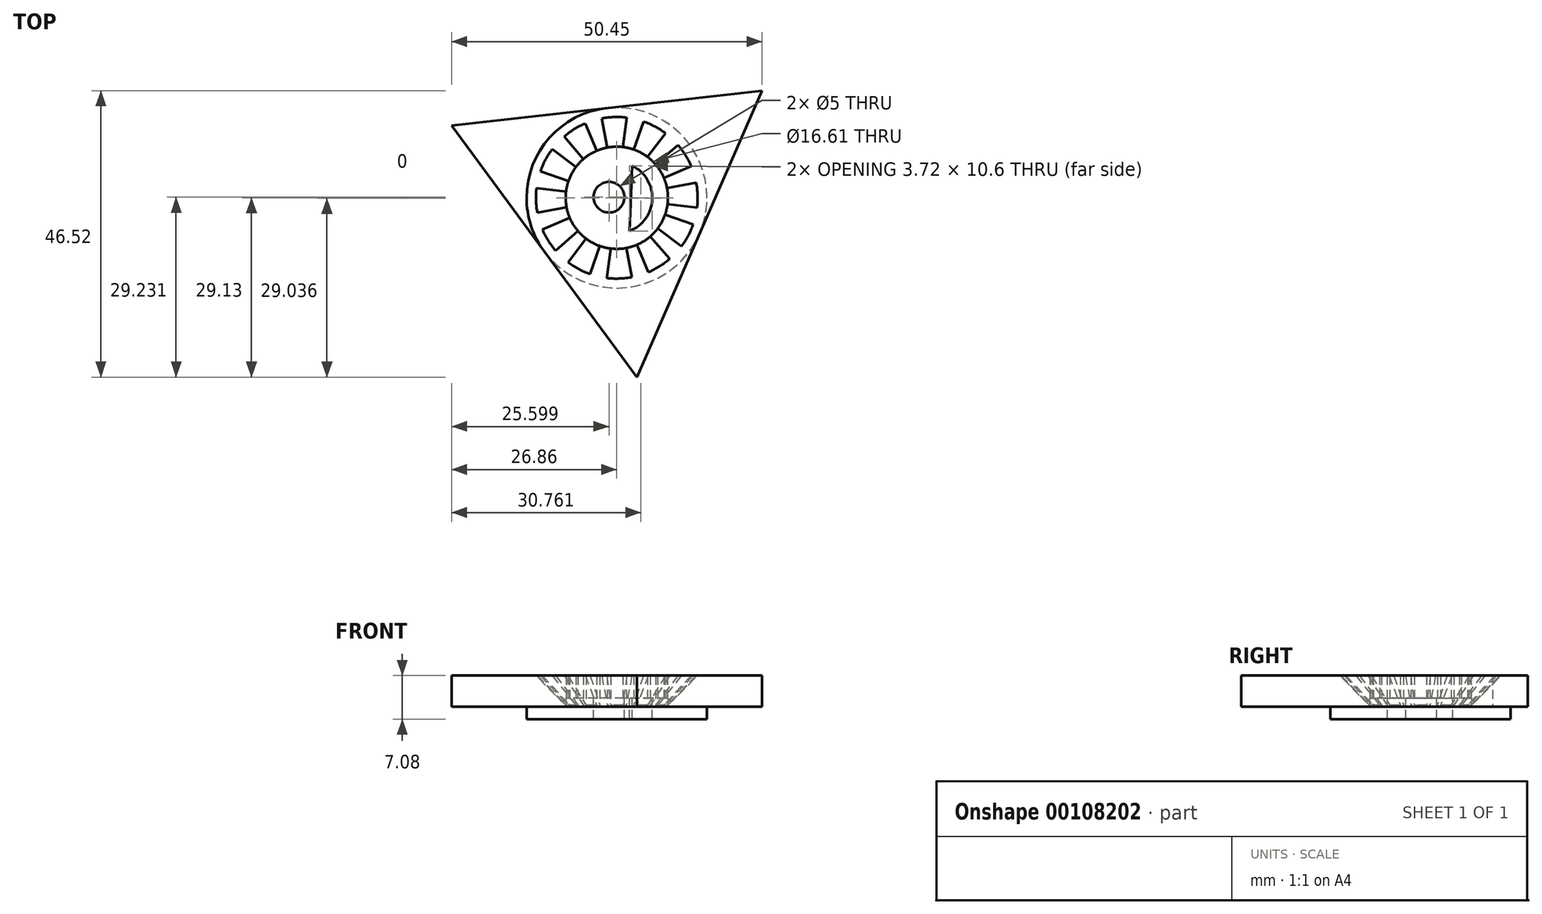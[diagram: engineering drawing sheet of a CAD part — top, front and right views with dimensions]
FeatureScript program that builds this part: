
annotation { "Feature Type Name" : "Feature", "Feature Type Description" : "" }
export const myFeature = defineFeature(function(context is Context, id is Id, definition is map)
    precondition{}
    {
        {
            var Q0;
            Q0=qCreatedBy(makeId("Top.planeOp"),FACE);
            var sketch = newSketch(context, id + "F0", { "sketchPlane" : qUnion([Q0])});
            skCircle(sketch, "E0", {"center": v(0, 0) * mm, "radius": 14.66 * mm});
            skCircle(sketch, "E1.cCircle", {"center": v(0, 0) * mm, "radius": 14.66 * mm, "construction": true});
            skLineSegment(sketch, "E1.0", {"start": v(23.6, 17.4) * mm, "end": v(3.27, -29.13) * mm});
            skLineSegment(sketch, "E1.1", {"start": v(3.27, -29.13) * mm, "end": v(-26.86, 11.73) * mm});
            skLineSegment(sketch, "E1.2", {"start": v(-26.86, 11.73) * mm, "end": v(23.6, 17.4) * mm});
            skPoint(sketch, "E1.0.midPoint", {"position": v(13.43, -5.87) * mm});
            skCircle(sketch, "E2", {"center": v(0, 0) * mm, "radius": 8.3 * mm});
            skSolve(sketch);
        }
        {
            var Q0;
            {var subQ0=sQuery(id+"F0.wireOp",EDGE,"E1.1");var subQ1=sQuery(id+"F0.wireOp",EDGE,"E0");var subQ2=makeQuery(id+"F0.imprint","INTERSECT",VERTEX,{"derivedFrom":[subQ1,subQ0]});Q0=makeQuery(id+"F0.imprint","IMPRINT",FACE,{"disambiguationData":[TD([[makeQuery(id+"F0.imprint","IMPRINT",EDGE,{"disambiguationData":[TD([[subQ2,1.0]])],"derivedFrom":subQ1}),-1.0]])]});}
            var Q1;
            {var subQ0=sQuery(id+"F0.wireOp",EDGE,"7ad4a74b-b42f-41d7-8abd-379b6c7fd1b9.3.0");Q1=makeQuery(id+"F0.imprint","IMPRINT",FACE,{"disambiguationData":[TD([[makeQuery(id+"F0.imprint","IMPRINT",EDGE,{"derivedFrom":subQ0}),-1.0]])]});}
            var Q2;
            {var subQ0=sQuery(id+"F0.wireOp",EDGE,"kC1Kmy56-I1pg-bns6-OiFE-b4c0AROArugu");Q2=makeQuery(id+"F0.imprint","IMPRINT",FACE,{"disambiguationData":[TD([[makeQuery(id+"F0.imprint","IMPRINT",EDGE,{"derivedFrom":subQ0}),-1.0]])]});}
            var Q3;
            {var subQ0=sQuery(id+"F0.wireOp",EDGE,"7ad4a74b-b42f-41d7-8abd-379b6c7fd1b9.7.0");Q3=makeQuery(id+"F0.imprint","IMPRINT",FACE,{"disambiguationData":[TD([[makeQuery(id+"F0.imprint","IMPRINT",EDGE,{"derivedFrom":subQ0}),-1.0]])]});}
            var Q4;
            {var subQ0=sQuery(id+"F0.wireOp",EDGE,"7ad4a74b-b42f-41d7-8abd-379b6c7fd1b9.6.0");Q4=makeQuery(id+"F0.imprint","IMPRINT",FACE,{"disambiguationData":[TD([[makeQuery(id+"F0.imprint","IMPRINT",EDGE,{"derivedFrom":subQ0}),-1.0]])]});}
            var Q5;
            {var subQ0=sQuery(id+"F0.wireOp",EDGE,"E1.1");var subQ1=sQuery(id+"F0.wireOp",EDGE,"E0");var subQ2=makeQuery(id+"F0.imprint","INTERSECT",VERTEX,{"derivedFrom":[subQ1,subQ0]});Q5=makeQuery(id+"F0.imprint","IMPRINT",FACE,{"disambiguationData":[TD([[makeQuery(id+"F0.imprint","IMPRINT",EDGE,{"disambiguationData":[TD([[subQ2,-1.0]])],"derivedFrom":subQ1}),-1.0]])]});}
            var Q6;
            {var subQ15=sQuery(id+"F0.wireOp",EDGE,"E0");var subQ18=makeQuery(id+"F0.imprint","INTERSECT",VERTEX,{"derivedFrom":[subQ15,sQuery(id+"F0.wireOp",EDGE,"E1.1")]});Q6=makeQuery(id+"F0.imprint","IMPRINT",FACE,{"disambiguationData":[TD([[makeQuery(id+"F0.imprint","IMPRINT",EDGE,{"disambiguationData":[TD([[subQ18,1.0]])],"derivedFrom":subQ15}),1.0]])]});}
            var Q7;
            {var subQ0=sQuery(id+"F0.wireOp",EDGE,"7ad4a74b-b42f-41d7-8abd-379b6c7fd1b9.8.0");Q7=makeQuery(id+"F0.imprint","IMPRINT",FACE,{"disambiguationData":[TD([[makeQuery(id+"F0.imprint","IMPRINT",EDGE,{"derivedFrom":subQ0}),-1.0]])]});}
            var Q8;
            {var subQ0=sQuery(id+"F0.wireOp",EDGE,"7ad4a74b-b42f-41d7-8abd-379b6c7fd1b9.1.0");Q8=makeQuery(id+"F0.imprint","IMPRINT",FACE,{"disambiguationData":[TD([[makeQuery(id+"F0.imprint","IMPRINT",EDGE,{"derivedFrom":subQ0}),-1.0]])]});}
            var Q9;
            {var subQ0=sQuery(id+"F0.wireOp",EDGE,"7ad4a74b-b42f-41d7-8abd-379b6c7fd1b9.5.0");Q9=makeQuery(id+"F0.imprint","IMPRINT",FACE,{"disambiguationData":[TD([[makeQuery(id+"F0.imprint","IMPRINT",EDGE,{"derivedFrom":subQ0}),-1.0]])]});}
            var Q10;
            {var subQ0=sQuery(id+"F0.wireOp",EDGE,"7ad4a74b-b42f-41d7-8abd-379b6c7fd1b9.10.0");Q10=makeQuery(id+"F0.imprint","IMPRINT",FACE,{"disambiguationData":[TD([[makeQuery(id+"F0.imprint","IMPRINT",EDGE,{"derivedFrom":subQ0}),-1.0]])]});}
            var Q11;
            {var subQ0=sQuery(id+"F0.wireOp",EDGE,"7ad4a74b-b42f-41d7-8abd-379b6c7fd1b9.11.0");Q11=makeQuery(id+"F0.imprint","IMPRINT",FACE,{"disambiguationData":[TD([[makeQuery(id+"F0.imprint","IMPRINT",EDGE,{"derivedFrom":subQ0}),-1.0]])]});}
            var Q12;
            {var subQ0=sQuery(id+"F0.wireOp",EDGE,"7ad4a74b-b42f-41d7-8abd-379b6c7fd1b9.4.0");Q12=makeQuery(id+"F0.imprint","IMPRINT",FACE,{"disambiguationData":[TD([[makeQuery(id+"F0.imprint","IMPRINT",EDGE,{"derivedFrom":subQ0}),-1.0]])]});}
            var Q13;
            {var subQ0=sQuery(id+"F0.wireOp",EDGE,"7ad4a74b-b42f-41d7-8abd-379b6c7fd1b9.9.0");Q13=makeQuery(id+"F0.imprint","IMPRINT",FACE,{"disambiguationData":[TD([[makeQuery(id+"F0.imprint","IMPRINT",EDGE,{"derivedFrom":subQ0}),-1.0]])]});}
            var Q14;
            {var subQ0=sQuery(id+"F0.wireOp",EDGE,"E1.2");var subQ1=sQuery(id+"F0.wireOp",EDGE,"E0");var subQ2=makeQuery(id+"F0.imprint","INTERSECT",VERTEX,{"derivedFrom":[subQ1,subQ0]});Q14=makeQuery(id+"F0.imprint","IMPRINT",FACE,{"disambiguationData":[TD([[makeQuery(id+"F0.imprint","IMPRINT",EDGE,{"disambiguationData":[TD([[subQ2,1.0]])],"derivedFrom":subQ1}),-1.0]])]});}
            var Q15;
            {var subQ0=sQuery(id+"F0.wireOp",EDGE,"7ad4a74b-b42f-41d7-8abd-379b6c7fd1b9.2.0");Q15=makeQuery(id+"F0.imprint","IMPRINT",FACE,{"disambiguationData":[TD([[makeQuery(id+"F0.imprint","IMPRINT",EDGE,{"derivedFrom":subQ0}),-1.0]])]});}
            extrude(context, id + "F1", {"entities" : qUnion([Q0, Q1, Q2, Q3, Q4, Q5, Q6, Q7, Q8, Q9, Q10, Q11, Q12, Q13, Q14, Q15]), "depth" : 5.08 * mm});
        }
        {
            var Q0;
            Q0=makeQuery(id+"F1.opExtrude","CAP_EDGE",EDGE,{"disambiguationData":[OSD([sQuery(id+"F0.wireOp",EDGE,"E2")])],"isStart":false});
            chamfer(context, id + "F2", {"entities" : qUnion([Q0]), "width" : 4.83 * mm, "tangentPropagation" : true});
        }
        {
            var Q0;
            Q0=makeQuery(id+"F1.opExtrude","CAP_FACE",FACE,{"disambiguationData":[OSD([sQuery(id+"F0.wireOp",EDGE,"E1.0"),sQuery(id+"F0.wireOp",EDGE,"E1.1"),sQuery(id+"F0.wireOp",EDGE,"E1.2"),sQuery(id+"F0.wireOp",EDGE,"E2")])],"isStart":true});
            var sketch = newSketch(context, id + "F3", { "sketchPlane" : qUnion([Q0])});
            skCircle(sketch, "E3.0", {"center": v(0, 0) * mm, "radius": 8.3 * mm});
            skLineSegment(sketch, "E3.1", {"start": v(-26.86, -11.73) * mm, "end": v(23.6, -17.4) * mm});
            skLineSegment(sketch, "E3.2", {"start": v(3.27, 29.13) * mm, "end": v(-26.86, -11.73) * mm});
            skLineSegment(sketch, "E3.3", {"start": v(23.6, -17.4) * mm, "end": v(3.27, 29.13) * mm});
            skCircle(sketch, "E4.0", {"center": v(0, 0) * mm, "radius": 14.66 * mm});
            skLineSegment(sketch, "E5", {"start": v(-5, 6.64) * mm, "end": v(-8.81, 11.71) * mm});
            skLineSegment(sketch, "E6", {"start": v(-6.3, 5.42) * mm, "end": v(-11.1, 9.57) * mm});
            skLineSegment(sketch, "E7.1.0", {"start": v(-8.16, 1.55) * mm, "end": v(-14.4, 2.73) * mm});
            skLineSegment(sketch, "E7.1.1", {"start": v(-7.64, 3.25) * mm, "end": v(-13.49, 5.74) * mm});
            skLineSegment(sketch, "E7.2.0", {"start": v(-7.84, -2.74) * mm, "end": v(-13.84, -4.83) * mm});
            skLineSegment(sketch, "E7.2.1", {"start": v(-8.24, -1) * mm, "end": v(-14.55, -1.78) * mm});
            skLineSegment(sketch, "E7.3.0", {"start": v(-5.42, -6.3) * mm, "end": v(-9.57, -11.1) * mm});
            skLineSegment(sketch, "E7.3.1", {"start": v(-6.64, -5) * mm, "end": v(-11.71, -8.81) * mm});
            skLineSegment(sketch, "E7.4.0", {"start": v(-1.55, -8.16) * mm, "end": v(-2.73, -14.4) * mm});
            skLineSegment(sketch, "E7.4.1", {"start": v(-3.25, -7.64) * mm, "end": v(-5.74, -13.49) * mm});
            skLineSegment(sketch, "E7.5.0", {"start": v(2.74, -7.84) * mm, "end": v(4.83, -13.84) * mm});
            skLineSegment(sketch, "E7.5.1", {"start": v(1, -8.24) * mm, "end": v(1.78, -14.55) * mm});
            skLineSegment(sketch, "E7.6.0", {"start": v(6.3, -5.42) * mm, "end": v(11.1, -9.57) * mm});
            skLineSegment(sketch, "E7.6.1", {"start": v(5, -6.64) * mm, "end": v(8.81, -11.71) * mm});
            skLineSegment(sketch, "E7.7.0", {"start": v(8.16, -1.55) * mm, "end": v(14.4, -2.73) * mm});
            skLineSegment(sketch, "E7.7.1", {"start": v(7.64, -3.25) * mm, "end": v(13.49, -5.74) * mm});
            skLineSegment(sketch, "E7.8.0", {"start": v(7.84, 2.74) * mm, "end": v(13.84, 4.83) * mm});
            skLineSegment(sketch, "E7.8.1", {"start": v(8.24, 1) * mm, "end": v(14.55, 1.78) * mm});
            skLineSegment(sketch, "E7.9.0", {"start": v(5.42, 6.3) * mm, "end": v(9.57, 11.1) * mm});
            skLineSegment(sketch, "E7.9.1", {"start": v(6.64, 5) * mm, "end": v(11.71, 8.81) * mm});
            skLineSegment(sketch, "E7.10.0", {"start": v(1.55, 8.16) * mm, "end": v(2.73, 14.4) * mm});
            skLineSegment(sketch, "E7.10.1", {"start": v(3.25, 7.64) * mm, "end": v(5.74, 13.49) * mm});
            skLineSegment(sketch, "E7.11.0", {"start": v(-2.74, 7.84) * mm, "end": v(-4.83, 13.84) * mm});
            skLineSegment(sketch, "E7.11.1", {"start": v(-1, 8.24) * mm, "end": v(-1.78, 14.55) * mm});
            skLineSegment(sketch, "E8", {"start": v(3.25, 7.64) * mm, "end": v(-3.25, -7.64) * mm});
            skSolve(sketch);
        }
        {
            var Q0;
            {var subQ0=sQuery(id+"F3.wireOp",EDGE,"E5");Q0=makeQuery(id+"F3.imprint","IMPRINT",FACE,{"disambiguationData":[TD([[makeQuery(id+"F3.imprint","IMPRINT",EDGE,{"derivedFrom":subQ0}),1.0]])]});}
            var Q1;
            {var subQ0=sQuery(id+"F3.wireOp",EDGE,"E7.11.0");Q1=makeQuery(id+"F3.imprint","IMPRINT",FACE,{"disambiguationData":[TD([[makeQuery(id+"F3.imprint","IMPRINT",EDGE,{"derivedFrom":subQ0}),-1.0]])]});}
            var Q2;
            {var subQ0=sQuery(id+"F3.wireOp",EDGE,"E7.10.0");Q2=makeQuery(id+"F3.imprint","IMPRINT",FACE,{"disambiguationData":[TD([[makeQuery(id+"F3.imprint","IMPRINT",EDGE,{"derivedFrom":subQ0}),-1.0]])]});}
            var Q3;
            {var subQ0=sQuery(id+"F3.wireOp",EDGE,"E7.9.0");Q3=makeQuery(id+"F3.imprint","IMPRINT",FACE,{"disambiguationData":[TD([[makeQuery(id+"F3.imprint","IMPRINT",EDGE,{"derivedFrom":subQ0}),-1.0]])]});}
            var Q4;
            {var subQ0=sQuery(id+"F3.wireOp",EDGE,"E7.8.0");Q4=makeQuery(id+"F3.imprint","IMPRINT",FACE,{"disambiguationData":[TD([[makeQuery(id+"F3.imprint","IMPRINT",EDGE,{"derivedFrom":subQ0}),-1.0]])]});}
            var Q5;
            {var subQ0=sQuery(id+"F3.wireOp",EDGE,"E7.7.0");Q5=makeQuery(id+"F3.imprint","IMPRINT",FACE,{"disambiguationData":[TD([[makeQuery(id+"F3.imprint","IMPRINT",EDGE,{"derivedFrom":subQ0}),-1.0]])]});}
            var Q6;
            {var subQ0=sQuery(id+"F3.wireOp",EDGE,"E7.6.0");Q6=makeQuery(id+"F3.imprint","IMPRINT",FACE,{"disambiguationData":[TD([[makeQuery(id+"F3.imprint","IMPRINT",EDGE,{"derivedFrom":subQ0}),-1.0]])]});}
            var Q7;
            {var subQ0=sQuery(id+"F3.wireOp",EDGE,"E7.5.0");Q7=makeQuery(id+"F3.imprint","IMPRINT",FACE,{"disambiguationData":[TD([[makeQuery(id+"F3.imprint","IMPRINT",EDGE,{"derivedFrom":subQ0}),-1.0]])]});}
            var Q8;
            {var subQ0=sQuery(id+"F3.wireOp",EDGE,"E7.4.0");Q8=makeQuery(id+"F3.imprint","IMPRINT",FACE,{"disambiguationData":[TD([[makeQuery(id+"F3.imprint","IMPRINT",EDGE,{"derivedFrom":subQ0}),-1.0]])]});}
            var Q9;
            {var subQ0=sQuery(id+"F3.wireOp",EDGE,"E7.3.0");Q9=makeQuery(id+"F3.imprint","IMPRINT",FACE,{"disambiguationData":[TD([[makeQuery(id+"F3.imprint","IMPRINT",EDGE,{"derivedFrom":subQ0}),-1.0]])]});}
            var Q10;
            {var subQ0=sQuery(id+"F3.wireOp",EDGE,"E7.2.0");Q10=makeQuery(id+"F3.imprint","IMPRINT",FACE,{"disambiguationData":[TD([[makeQuery(id+"F3.imprint","IMPRINT",EDGE,{"derivedFrom":subQ0}),-1.0]])]});}
            var Q11;
            {var subQ0=sQuery(id+"F3.wireOp",EDGE,"E7.1.0");Q11=makeQuery(id+"F3.imprint","IMPRINT",FACE,{"disambiguationData":[TD([[makeQuery(id+"F3.imprint","IMPRINT",EDGE,{"derivedFrom":subQ0}),-1.0]])]});}
            var Q12;
            Q12=makeQuery(id+"F1.opExtrude","CAP_FACE",FACE,{"disambiguationData":[OSD([sQuery(id+"F0.wireOp",EDGE,"E1.0"),sQuery(id+"F0.wireOp",EDGE,"E1.1"),sQuery(id+"F0.wireOp",EDGE,"E1.2"),sQuery(id+"F0.wireOp",EDGE,"E2")])],"isStart":false});
            extrude(context, id + "F4", {"entities" : qUnion([Q0, Q1, Q2, Q3, Q4, Q5, Q6, Q7, Q8, Q9, Q10, Q11]), "operationType" : NewBodyOperationType.ADD, "endBound" : BoundingType.UP_TO_SURFACE, "oppositeDirection" : true, "endBoundEntityFace" : qUnion([Q12]), "depth" : 25.4 * mm});
        }
        {
            var Q0;
            {var subQ0=sQuery(id+"F3.wireOp",EDGE,"E3.0");var subQ7=makeQuery(id+"F3.imprint","INTERSECT",VERTEX,{"derivedFrom":[subQ0,sQuery(id+"F3.wireOp",EDGE,"E7.7.0")]});Q0=makeQuery(id+"F3.imprint","IMPRINT",FACE,{"disambiguationData":[TD([[makeQuery(id+"F3.imprint","IMPRINT",EDGE,{"disambiguationData":[TD([[subQ7,-1.0]])],"derivedFrom":subQ0}),-1.0]])]});}
            var Q1;
            {var subQ4=sQuery(id+"F3.wireOp",EDGE,"E8");Q1=makeQuery(id+"F3.imprint","IMPRINT",FACE,{"disambiguationData":[TD([[makeQuery(id+"F3.imprint","IMPRINT",EDGE,{"derivedFrom":subQ4}),-1.0]])]});}
            extrude(context, id + "F5", {"entities" : qUnion([Q0, Q1]), "oppositeDirection" : true, "depth" : 1.4 * mm});
        }
        {
            var Q0;
            {var subQ0=sQuery(id+"F3.wireOp",EDGE,"E7.11.0");Q0=makeQuery(id+"F3.imprint","IMPRINT",FACE,{"disambiguationData":[TD([[makeQuery(id+"F3.imprint","IMPRINT",EDGE,{"derivedFrom":subQ0}),-1.0]])]});}
            var Q1;
            {var subQ0=sQuery(id+"F3.wireOp",EDGE,"E5");Q1=makeQuery(id+"F3.imprint","IMPRINT",FACE,{"disambiguationData":[TD([[makeQuery(id+"F3.imprint","IMPRINT",EDGE,{"derivedFrom":subQ0}),-1.0]])]});}
            var Q2;
            {var subQ0=sQuery(id+"F3.wireOp",EDGE,"E7.10.0");Q2=makeQuery(id+"F3.imprint","IMPRINT",FACE,{"disambiguationData":[TD([[makeQuery(id+"F3.imprint","IMPRINT",EDGE,{"derivedFrom":subQ0}),1.0]])]});}
            var Q3;
            {var subQ0=sQuery(id+"F3.wireOp",EDGE,"E7.10.0");Q3=makeQuery(id+"F3.imprint","IMPRINT",FACE,{"disambiguationData":[TD([[makeQuery(id+"F3.imprint","IMPRINT",EDGE,{"derivedFrom":subQ0}),-1.0]])]});}
            var Q4;
            {var subQ0=sQuery(id+"F3.wireOp",EDGE,"E7.9.0");Q4=makeQuery(id+"F3.imprint","IMPRINT",FACE,{"disambiguationData":[TD([[makeQuery(id+"F3.imprint","IMPRINT",EDGE,{"derivedFrom":subQ0}),1.0]])]});}
            var Q5;
            {var subQ0=sQuery(id+"F3.wireOp",EDGE,"E7.9.0");Q5=makeQuery(id+"F3.imprint","IMPRINT",FACE,{"disambiguationData":[TD([[makeQuery(id+"F3.imprint","IMPRINT",EDGE,{"derivedFrom":subQ0}),-1.0]])]});}
            var Q6;
            {var subQ0=sQuery(id+"F3.wireOp",EDGE,"E7.8.0");Q6=makeQuery(id+"F3.imprint","IMPRINT",FACE,{"disambiguationData":[TD([[makeQuery(id+"F3.imprint","IMPRINT",EDGE,{"derivedFrom":subQ0}),1.0]])]});}
            var Q7;
            {var subQ0=sQuery(id+"F3.wireOp",EDGE,"E7.8.0");Q7=makeQuery(id+"F3.imprint","IMPRINT",FACE,{"disambiguationData":[TD([[makeQuery(id+"F3.imprint","IMPRINT",EDGE,{"derivedFrom":subQ0}),-1.0]])]});}
            var Q8;
            {var subQ0=sQuery(id+"F3.wireOp",EDGE,"E7.7.0");Q8=makeQuery(id+"F3.imprint","IMPRINT",FACE,{"disambiguationData":[TD([[makeQuery(id+"F3.imprint","IMPRINT",EDGE,{"derivedFrom":subQ0}),1.0]])]});}
            var Q9;
            {var subQ0=sQuery(id+"F3.wireOp",EDGE,"E7.7.0");Q9=makeQuery(id+"F3.imprint","IMPRINT",FACE,{"disambiguationData":[TD([[makeQuery(id+"F3.imprint","IMPRINT",EDGE,{"derivedFrom":subQ0}),-1.0]])]});}
            var Q10;
            {var subQ0=sQuery(id+"F3.wireOp",EDGE,"E7.6.0");Q10=makeQuery(id+"F3.imprint","IMPRINT",FACE,{"disambiguationData":[TD([[makeQuery(id+"F3.imprint","IMPRINT",EDGE,{"derivedFrom":subQ0}),1.0]])]});}
            var Q11;
            {var subQ0=sQuery(id+"F3.wireOp",EDGE,"E7.6.0");Q11=makeQuery(id+"F3.imprint","IMPRINT",FACE,{"disambiguationData":[TD([[makeQuery(id+"F3.imprint","IMPRINT",EDGE,{"derivedFrom":subQ0}),-1.0]])]});}
            var Q12;
            {var subQ0=sQuery(id+"F3.wireOp",EDGE,"E7.5.0");Q12=makeQuery(id+"F3.imprint","IMPRINT",FACE,{"disambiguationData":[TD([[makeQuery(id+"F3.imprint","IMPRINT",EDGE,{"derivedFrom":subQ0}),1.0]])]});}
            var Q13;
            {var subQ0=sQuery(id+"F3.wireOp",EDGE,"E7.5.0");Q13=makeQuery(id+"F3.imprint","IMPRINT",FACE,{"disambiguationData":[TD([[makeQuery(id+"F3.imprint","IMPRINT",EDGE,{"derivedFrom":subQ0}),-1.0]])]});}
            var Q14;
            {var subQ3=sQuery(id+"F3.wireOp",EDGE,"E7.4.0");Q14=makeQuery(id+"F3.imprint","IMPRINT",FACE,{"disambiguationData":[TD([[makeQuery(id+"F3.imprint","IMPRINT",EDGE,{"derivedFrom":subQ3}),1.0]])]});}
            var Q15;
            {var subQ0=sQuery(id+"F3.wireOp",EDGE,"E7.4.0");Q15=makeQuery(id+"F3.imprint","IMPRINT",FACE,{"disambiguationData":[TD([[makeQuery(id+"F3.imprint","IMPRINT",EDGE,{"derivedFrom":subQ0}),-1.0]])]});}
            var Q16;
            {var subQ0=sQuery(id+"F3.wireOp",EDGE,"E7.3.0");Q16=makeQuery(id+"F3.imprint","IMPRINT",FACE,{"disambiguationData":[TD([[makeQuery(id+"F3.imprint","IMPRINT",EDGE,{"derivedFrom":subQ0}),1.0]])]});}
            var Q17;
            {var subQ0=sQuery(id+"F3.wireOp",EDGE,"E7.3.0");Q17=makeQuery(id+"F3.imprint","IMPRINT",FACE,{"disambiguationData":[TD([[makeQuery(id+"F3.imprint","IMPRINT",EDGE,{"derivedFrom":subQ0}),-1.0]])]});}
            var Q18;
            {var subQ0=sQuery(id+"F3.wireOp",EDGE,"E7.2.0");Q18=makeQuery(id+"F3.imprint","IMPRINT",FACE,{"disambiguationData":[TD([[makeQuery(id+"F3.imprint","IMPRINT",EDGE,{"derivedFrom":subQ0}),1.0]])]});}
            var Q19;
            {var subQ0=sQuery(id+"F3.wireOp",EDGE,"E7.2.0");Q19=makeQuery(id+"F3.imprint","IMPRINT",FACE,{"disambiguationData":[TD([[makeQuery(id+"F3.imprint","IMPRINT",EDGE,{"derivedFrom":subQ0}),-1.0]])]});}
            var Q20;
            {var subQ0=sQuery(id+"F3.wireOp",EDGE,"E7.1.0");Q20=makeQuery(id+"F3.imprint","IMPRINT",FACE,{"disambiguationData":[TD([[makeQuery(id+"F3.imprint","IMPRINT",EDGE,{"derivedFrom":subQ0}),1.0]])]});}
            var Q21;
            {var subQ0=sQuery(id+"F3.wireOp",EDGE,"E7.1.0");Q21=makeQuery(id+"F3.imprint","IMPRINT",FACE,{"disambiguationData":[TD([[makeQuery(id+"F3.imprint","IMPRINT",EDGE,{"derivedFrom":subQ0}),-1.0]])]});}
            var Q22;
            {var subQ0=sQuery(id+"F3.wireOp",EDGE,"E6");Q22=makeQuery(id+"F3.imprint","IMPRINT",FACE,{"disambiguationData":[TD([[makeQuery(id+"F3.imprint","IMPRINT",EDGE,{"derivedFrom":subQ0}),1.0]])]});}
            var Q23;
            {var subQ0=sQuery(id+"F3.wireOp",EDGE,"E5");Q23=makeQuery(id+"F3.imprint","IMPRINT",FACE,{"disambiguationData":[TD([[makeQuery(id+"F3.imprint","IMPRINT",EDGE,{"derivedFrom":subQ0}),1.0]])]});}
            var Q24;
            {var subQ0=sQuery(id+"F3.wireOp",EDGE,"E3.0");var subQ7=makeQuery(id+"F3.imprint","INTERSECT",VERTEX,{"derivedFrom":[subQ0,sQuery(id+"F3.wireOp",EDGE,"E7.7.0")]});Q24=makeQuery(id+"F3.imprint","IMPRINT",FACE,{"disambiguationData":[TD([[makeQuery(id+"F3.imprint","IMPRINT",EDGE,{"disambiguationData":[TD([[subQ7,-1.0]])],"derivedFrom":subQ0}),-1.0]])]});}
            var Q25;
            {var subQ4=sQuery(id+"F3.wireOp",EDGE,"E8");Q25=makeQuery(id+"F3.imprint","IMPRINT",FACE,{"disambiguationData":[TD([[makeQuery(id+"F3.imprint","IMPRINT",EDGE,{"derivedFrom":subQ4}),-1.0]])]});}
            extrude(context, id + "F6", {"entities" : qUnion([Q0, Q1, Q2, Q3, Q4, Q5, Q6, Q7, Q8, Q9, Q10, Q11, Q12, Q13, Q14, Q15, Q16, Q17, Q18, Q19, Q20, Q21, Q22, Q23, Q24, Q25]), "depth" : 2 * mm});
        }
        {
            var Q0;
            Q0=makeQuery(id+"F5.opExtrude","CAP_FACE",FACE,{"disambiguationData":[OSD([sQuery(id+"F3.wireOp",EDGE,"E3.0")])],"isStart":false});
            var sketch = newSketch(context, id + "F7", { "sketchPlane" : qUnion([Q0])});
            skCircle(sketch, "E9.0", {"center": v(0, 0) * mm, "radius": 8.3 * mm});
            skCircle(sketch, "E10.0", {"center": v(0, 0) * mm, "radius": 5.77 * mm});
            skLineSegment(sketch, "E11", {"start": v(2.04, -5.4) * mm, "end": v(2.48, 5.2) * mm});
            skCircle(sketch, "E12", {"center": v(-1.26, 0.1) * mm, "radius": 2.5 * mm});
            skLineSegment(sketch, "E13", {"start": v(5.75, -0.4) * mm, "end": v(-5.75, 0.42) * mm});
            skSolve(sketch);
        }
        {
            var Q0;
            {var subQ0=sQuery(id+"F7.wireOp",EDGE,"E11");Q0=makeQuery(id+"F7.imprint","IMPRINT",FACE,{"disambiguationData":[TD([[makeQuery(id+"F7.imprint","IMPRINT",EDGE,{"derivedFrom":subQ0}),-1.0]])]});}
            var Q1;
            Q1=makeQuery(id+"F7.imprint","IMPRINT",FACE,{"disambiguationData":[TD([[makeQuery(id+"F7.imprint","IMPRINT",EDGE,{"derivedFrom":sQuery(id+"F7.wireOp",EDGE,"E12")}),1.0]])]});
            extrude(context, id + "F8", {"entities" : qUnion([Q0, Q1]), "operationType" : NewBodyOperationType.REMOVE, "oppositeDirection" : true, "depth" : 25.4 * mm});
        }
        {
            var Q0;
            Q0=makeQuery(id+"F1.opExtrude","SWEPT_BODY",BODY,{"disambiguationData":[OSD([sQuery(id+"F0.wireOp",EDGE,"E1.0"),sQuery(id+"F0.wireOp",EDGE,"E1.1"),sQuery(id+"F0.wireOp",EDGE,"E1.2"),sQuery(id+"F0.wireOp",EDGE,"E2")])]});
            transform(context, id + "F9", {"entities" : qUnion([Q0]), "transformType" : TransformType.TRANSLATION_3D, "dx" : 0 * mm, "dy" : 0 * mm, "dz" : 0 * mm, "makeCopy" : true});
        }
        {
            var Q0;
            Q0=makeQuery(id+"F9.opPattern","COPY",BODY,{"derivedFrom":makeQuery(id+"F1.opExtrude","SWEPT_BODY",BODY,{"disambiguationData":[OSD([sQuery(id+"F0.wireOp",EDGE,"E1.0"),sQuery(id+"F0.wireOp",EDGE,"E1.1"),sQuery(id+"F0.wireOp",EDGE,"E1.2"),sQuery(id+"F0.wireOp",EDGE,"E2")])]}),"instanceName":"1"});
            deleteBodies(context, id + "F10", {"entities" : qUnion([Q0])});
        }
    });
